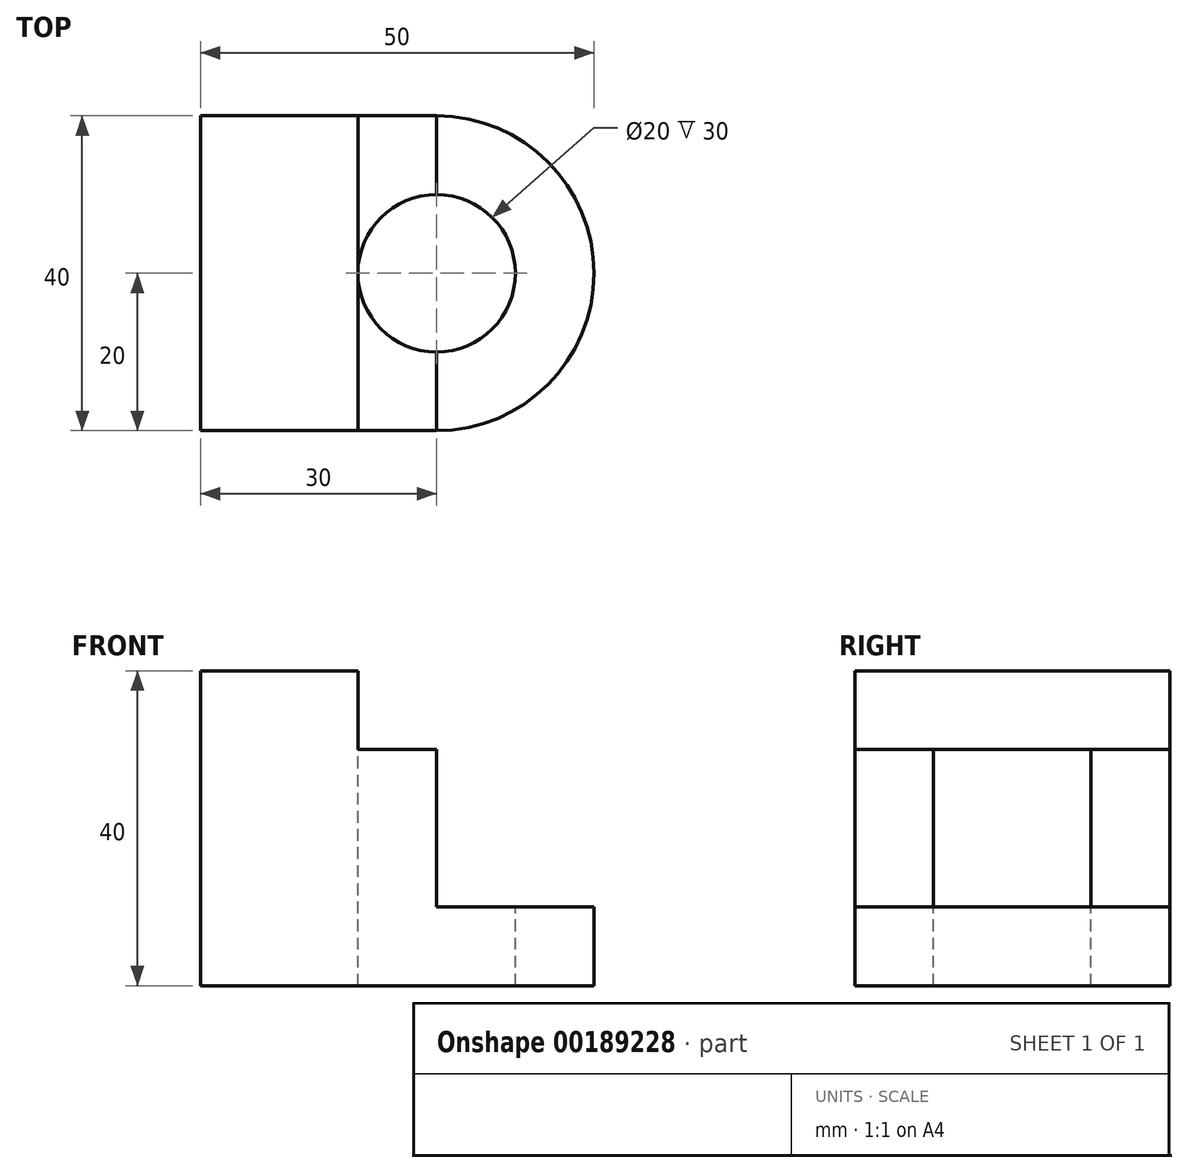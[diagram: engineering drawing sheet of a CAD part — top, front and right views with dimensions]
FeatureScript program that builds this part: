
annotation { "Feature Type Name" : "Feature", "Feature Type Description" : "" }
export const myFeature = defineFeature(function(context is Context, id is Id, definition is map)
    precondition{}
    {
        {
            var Q0;
            Q0=qCreatedBy(makeId("Front.planeOp"),FACE);
            var sketch = newSketch(context, id + "F0", { "sketchPlane" : qUnion([Q0])});
            skLineSegment(sketch, "E0", {"start": v(0, 0) * mm, "end": v(0, 40) * mm});
            skLineSegment(sketch, "E1", {"start": v(0, 40) * mm, "end": v(20, 40) * mm});
            skLineSegment(sketch, "E2", {"start": v(20, 40) * mm, "end": v(20, 30) * mm});
            skLineSegment(sketch, "E3", {"start": v(20, 30) * mm, "end": v(30, 30) * mm});
            skLineSegment(sketch, "E4", {"start": v(30, 30) * mm, "end": v(30, 10) * mm});
            skLineSegment(sketch, "E5", {"start": v(30, 10) * mm, "end": v(50, 10) * mm});
            skLineSegment(sketch, "E6", {"start": v(50, 10) * mm, "end": v(50, 0) * mm});
            skLineSegment(sketch, "E7", {"start": v(50, 0) * mm, "end": v(0, 0) * mm});
            skSolve(sketch);
        }
        {
            var Q0;
            Q0=makeQuery(id+"F0.imprint","IMPRINT",FACE,{"disambiguationData":[TD([[makeQuery(id+"F0.imprint","IMPRINT",EDGE,{"derivedFrom":sQuery(id+"F0.wireOp",EDGE,"E0")}),-1.0]])]});
            extrude(context, id + "F1", {"entities" : qUnion([Q0]), "endBound" : BoundingType.SYMMETRIC, "depth" : 40 * mm});
        }
        {
            var Q0;
            Q0=makeQuery(id+"F1.opExtrude","CAP_EDGE",EDGE,{"disambiguationData":[OSD([sQuery(id+"F0.wireOp",EDGE,"E6")])],"isStart":false});
            var Q1;
            Q1=makeQuery(id+"F1.opExtrude","CAP_EDGE",EDGE,{"disambiguationData":[OSD([sQuery(id+"F0.wireOp",EDGE,"E6")])],"isStart":true});
            fillet(context, id + "F2", {"entities" : qUnion([Q0, Q1]), "radius" : 20 * mm, "tangentPropagation" : true, "allowEdgeOverflow" : false});
        }
        {
            var Q0;
            Q0=makeQuery(id+"F1.opExtrude","SWEPT_FACE",FACE,{"disambiguationData":[OSD([sQuery(id+"F0.wireOp",EDGE,"E3")])]});
            var sketch = newSketch(context, id + "F3", { "sketchPlane" : qUnion([Q0])});
            skCircle(sketch, "E8", {"center": v(30, 0) * mm, "radius": 10 * mm});
            skSolve(sketch);
        }
        {
            var Q0;
            {var subQ0=sQuery(id+"F3.wireOp",EDGE,"E8");var subQ1=sQuery(id+"F0.wireOp",EDGE,"E3");var subQ2=makeQuery(id+"F3.imprint","INTERSECT",VERTEX,{"derivedFrom":[makeQuery(id+"F1.opExtrude","SWEPT_EDGE",EDGE,{"disambiguationData":[OSD([sQuery(id+"F0.wireOp",EDGE,"E2"),subQ1])]}),subQ0]});Q0=makeQuery(id+"F3.imprint","IMPRINT",FACE,{"disambiguationData":[TD([[makeQuery(id+"F3.imprint","IMPRINT",EDGE,{"disambiguationData":[TD([[subQ2,1.0]])],"derivedFrom":subQ0}),1.0]])]});}
            var Q1;
            {var subQ0=sQuery(id+"F3.wireOp",EDGE,"E8");var subQ1=makeQuery(id+"F1.opExtrude","SWEPT_EDGE",EDGE,{"disambiguationData":[OSD([sQuery(id+"F0.wireOp",EDGE,"E3"),sQuery(id+"F0.wireOp",EDGE,"E4")])]});var subQ2=makeQuery(id+"F3.imprint","INTERSECT",VERTEX,{"disambiguationData":[OD(0.0)],"derivedFrom":[subQ1,subQ0]});Q1=makeQuery(id+"F3.imprint","IMPRINT",FACE,{"disambiguationData":[TD([[makeQuery(id+"F3.imprint","IMPRINT",EDGE,{"disambiguationData":[TD([[subQ2,1.0]])],"derivedFrom":subQ0}),1.0]])]});}
            extrude(context, id + "F4", {"entities" : qUnion([Q0, Q1]), "operationType" : NewBodyOperationType.REMOVE, "endBound" : BoundingType.THROUGH_ALL, "oppositeDirection" : true, "depth" : 25 * mm});
        }
    });
